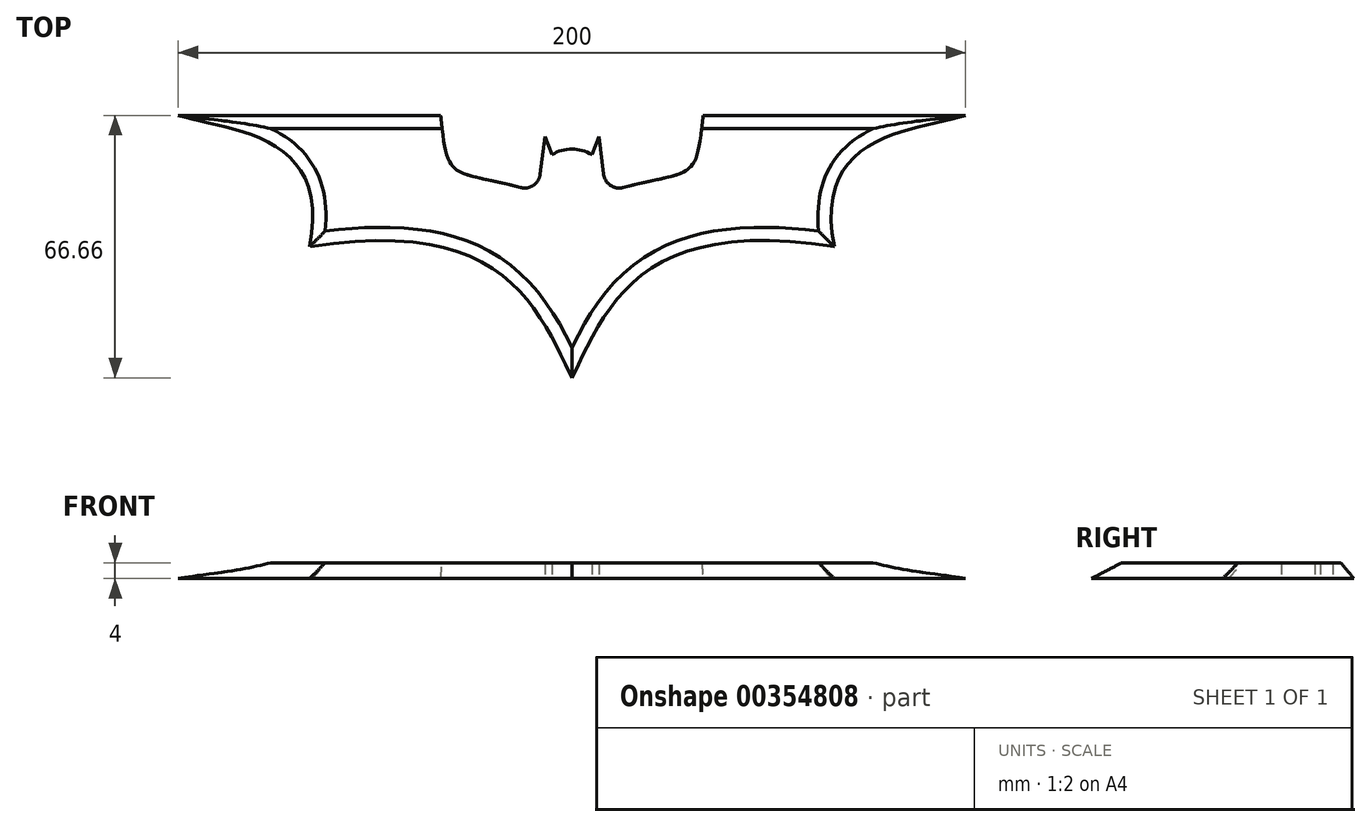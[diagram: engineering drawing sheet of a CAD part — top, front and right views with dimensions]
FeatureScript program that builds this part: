
annotation { "Feature Type Name" : "Feature", "Feature Type Description" : "" }
export const myFeature = defineFeature(function(context is Context, id is Id, definition is map)
    precondition{}
    {
        {
            assignVariable(context, id + "F0", {"name" : "thickness", "anyValue" : 2});
        }
        {
            var Q0;
            Q0=qCreatedBy(makeId("Top.planeOp"),FACE);
            var sketch = newSketch(context, id + "F1", { "sketchPlane" : qUnion([Q0])});
            skLineSegment(sketch, "E0", {"start": v(-50, 0) * mm, "end": v(-16.67, 0) * mm});
            skFitSpline(sketch, "E1", {"points": [v(-50, 0) * mm, v(-33.33, -16.67) * mm], "startDerivative": vector(19.44, -5.95) * mm, "endDerivative": vector(-8.63, -43.66) * mm});
            skFitSpline(sketch, "E2", {"points": [v(-33.33, -16.67) * mm, v(0, -33.33) * mm], "startDerivative": vector(72.06, 11.18) * mm, "endDerivative": vector(14.25, -29.82) * mm});
            skLineSegment(sketch, "E3", {"start": v(-3.43, -2.66) * mm, "end": v(-4.02, -7.47) * mm});
            skFitSpline(sketch, "E4", {"points": [v(-16.67, 0) * mm, v(-4.3, -9.77) * mm], "startDerivative": vector(2.79, -27.6) * mm, "endDerivative": vector(33.49, -9.74) * mm});
            skLineSegment(sketch, "E5", {"start": v(-3.43, -2.66) * mm, "end": v(-2.53, -4.98) * mm});
            skLineSegment(sketch, "E6.MirrorCS", {"start": v(3.43, -2.66) * mm, "end": v(4.02, -7.47) * mm});
            skFitSpline(sketch, "E7.MirrorCS", {"points": [v(16.67, 0) * mm, v(4.3, -9.77) * mm], "startDerivative": vector(-2.79, -27.6) * mm, "endDerivative": vector(-33.49, -9.74) * mm});
            skLineSegment(sketch, "E8.MirrorCS", {"start": v(3.43, -2.66) * mm, "end": v(2.53, -4.98) * mm});
            skLineSegment(sketch, "E9.MirrorCS", {"start": v(50, 0) * mm, "end": v(16.67, 0) * mm});
            skFitSpline(sketch, "E10.MirrorCS", {"points": [v(50, 0) * mm, v(33.33, -16.67) * mm], "startDerivative": vector(-19.44, -5.95) * mm, "endDerivative": vector(8.63, -43.66) * mm});
            skFitSpline(sketch, "E11.MirrorCS", {"points": [v(33.33, -16.67) * mm, v(0, -33.33) * mm], "startDerivative": vector(-72.06, 11.18) * mm, "endDerivative": vector(-14.25, -29.82) * mm});
            skArc(sketch, "E12", {"start": v(2.53, -4.98) * mm, "mid": v(0, -4.3) * mm, "end": v(-2.53, -4.98) * mm});
            skLineSegment(sketch, "E13", {"start": v(-33.33, -16.67) * mm, "end": v(-32.03, -10.1) * mm, "construction": true});
            skLineSegment(sketch, "E14", {"start": v(-33.33, -16.67) * mm, "end": v(-32, -16.46) * mm, "construction": true});
            skArc(sketch, "E15.filletArc", {"start": v(-6.5, -9.17) * mm, "mid": v(-4.88, -8.88) * mm, "end": v(-4.02, -7.47) * mm});
            skArc(sketch, "E16.filletArc", {"start": v(4.02, -7.47) * mm, "mid": v(4.88, -8.88) * mm, "end": v(6.5, -9.17) * mm});
            skLineSegment(sketch, "E17.bottom", {"start": v(-16.67, 0) * mm, "end": v(-33.33, 0) * mm, "construction": true});
            skLineSegment(sketch, "E17.top", {"start": v(-16.67, -16.67) * mm, "end": v(-33.33, -16.67) * mm, "construction": true});
            skLineSegment(sketch, "E17.left", {"start": v(-16.67, 0) * mm, "end": v(-16.67, -16.67) * mm, "construction": true});
            skLineSegment(sketch, "E17.right", {"start": v(-33.33, 0) * mm, "end": v(-33.33, -16.67) * mm, "construction": true});
            skSolve(sketch);
        }
        {
            var Q0;
            Q0=makeQuery(id+"F1.imprint","IMPRINT",FACE,{"disambiguationData":[TD([[makeQuery(id+"F1.imprint","IMPRINT",EDGE,{"derivedFrom":sQuery(id+"F1.wireOp",EDGE,"E0")}),-1.0]])]});
            extrude(context, id + "F2", {"entities" : qUnion([Q0]), "depth" : getVariable(context, 'thickness') * mm});
        }
        {
            var Q0;
            Q0=makeQuery(id+"F2.opExtrude","CAP_EDGE",EDGE,{"disambiguationData":[OSD([sQuery(id+"F1.wireOp",EDGE,"E1")])],"isStart":false});
            var Q1;
            Q1=makeQuery(id+"F2.opExtrude","CAP_EDGE",EDGE,{"disambiguationData":[OSD([sQuery(id+"F1.wireOp",EDGE,"E0")])],"isStart":false});
            var Q2;
            Q2=makeQuery(id+"F2.opExtrude","CAP_EDGE",EDGE,{"disambiguationData":[OSD([sQuery(id+"F1.wireOp",EDGE,"E2")])],"isStart":false});
            var Q3;
            Q3=makeQuery(id+"F2.opExtrude","CAP_EDGE",EDGE,{"disambiguationData":[OSD([sQuery(id+"F1.wireOp",EDGE,"E11.MirrorCS")])],"isStart":false});
            var Q4;
            Q4=makeQuery(id+"F2.opExtrude","CAP_EDGE",EDGE,{"disambiguationData":[OSD([sQuery(id+"F1.wireOp",EDGE,"E10.MirrorCS")])],"isStart":false});
            var Q5;
            Q5=makeQuery(id+"F2.opExtrude","CAP_EDGE",EDGE,{"disambiguationData":[OSD([sQuery(id+"F1.wireOp",EDGE,"E9.MirrorCS")])],"isStart":false});
            chamfer(context, id + "F3", {"entities" : qUnion([Q0, Q1, Q2, Q3, Q4, Q5]), "chamferType" : ChamferType.OFFSET_ANGLE, "width" : (getVariable(context, 'thickness')) * mm, "oppositeDirection" : true, "angle" : 40 * degree, "tangentPropagation" : true});
        }
        {
            var Q0;
            Q0=makeQuery(id+"F2.opExtrude","SWEPT_BODY",BODY,{"disambiguationData":[OSD([sQuery(id+"F1.wireOp",EDGE,"E0"),sQuery(id+"F1.wireOp",EDGE,"E1"),sQuery(id+"F1.wireOp",EDGE,"E2"),sQuery(id+"F1.wireOp",EDGE,"E3"),sQuery(id+"F1.wireOp",EDGE,"E4"),sQuery(id+"F1.wireOp",EDGE,"E5"),sQuery(id+"F1.wireOp",EDGE,"E6.MirrorCS"),sQuery(id+"F1.wireOp",EDGE,"E7.MirrorCS"),sQuery(id+"F1.wireOp",EDGE,"E8.MirrorCS"),sQuery(id+"F1.wireOp",EDGE,"E9.MirrorCS"),sQuery(id+"F1.wireOp",EDGE,"E10.MirrorCS"),sQuery(id+"F1.wireOp",EDGE,"E11.MirrorCS"),sQuery(id+"F1.wireOp",EDGE,"E12"),sQuery(id+"F1.wireOp",EDGE,"E15.filletArc"),sQuery(id+"F1.wireOp",EDGE,"E16.filletArc")])]});
            var Q1;
            {var subQ0=sQuery(id+"F1.wireOp",EDGE,"E11.MirrorCS");var subQ1=sQuery(id+"F1.wireOp",EDGE,"E2");Q1=makeQuery(id+"F3.opChamfer","BLEND_VERTEX",VERTEX,{"blendedFrom":[makeQuery(id+"F2.opExtrude","CAP_EDGE",EDGE,{"disambiguationData":[OSD([subQ1])],"isStart":false}),makeQuery(id+"F2.opExtrude","CAP_EDGE",EDGE,{"disambiguationData":[OSD([subQ0])],"isStart":false}),makeQuery(id+"F2.opExtrude","CAP_FACE",FACE,{"disambiguationData":[OSD([sQuery(id+"F1.wireOp",EDGE,"E0"),sQuery(id+"F1.wireOp",EDGE,"E1"),subQ1,sQuery(id+"F1.wireOp",EDGE,"E3"),sQuery(id+"F1.wireOp",EDGE,"E4"),sQuery(id+"F1.wireOp",EDGE,"E5"),sQuery(id+"F1.wireOp",EDGE,"E6.MirrorCS"),sQuery(id+"F1.wireOp",EDGE,"E7.MirrorCS"),sQuery(id+"F1.wireOp",EDGE,"E8.MirrorCS"),sQuery(id+"F1.wireOp",EDGE,"E9.MirrorCS"),sQuery(id+"F1.wireOp",EDGE,"E10.MirrorCS"),subQ0,sQuery(id+"F1.wireOp",EDGE,"E12"),sQuery(id+"F1.wireOp",EDGE,"E15.filletArc"),sQuery(id+"F1.wireOp",EDGE,"E16.filletArc")])],"isStart":true})],"blendedInto":[makeQuery(id+"F2.opExtrude","CAP_FACE",FACE,{"disambiguationData":[OSD([sQuery(id+"F1.wireOp",EDGE,"E0"),sQuery(id+"F1.wireOp",EDGE,"E1"),subQ1,sQuery(id+"F1.wireOp",EDGE,"E3"),sQuery(id+"F1.wireOp",EDGE,"E4"),sQuery(id+"F1.wireOp",EDGE,"E5"),sQuery(id+"F1.wireOp",EDGE,"E6.MirrorCS"),sQuery(id+"F1.wireOp",EDGE,"E7.MirrorCS"),sQuery(id+"F1.wireOp",EDGE,"E8.MirrorCS"),sQuery(id+"F1.wireOp",EDGE,"E9.MirrorCS"),sQuery(id+"F1.wireOp",EDGE,"E10.MirrorCS"),subQ0,sQuery(id+"F1.wireOp",EDGE,"E12"),sQuery(id+"F1.wireOp",EDGE,"E15.filletArc"),sQuery(id+"F1.wireOp",EDGE,"E16.filletArc")])],"isStart":true})]});}
            transform(context, id + "F4", {"entities" : qUnion([Q0]), "transformType" : TransformType.SCALE_UNIFORMLY, "scale" : 2, "scalePoint" : qUnion([Q1]), "makeCopy" : false});
        }
    });
